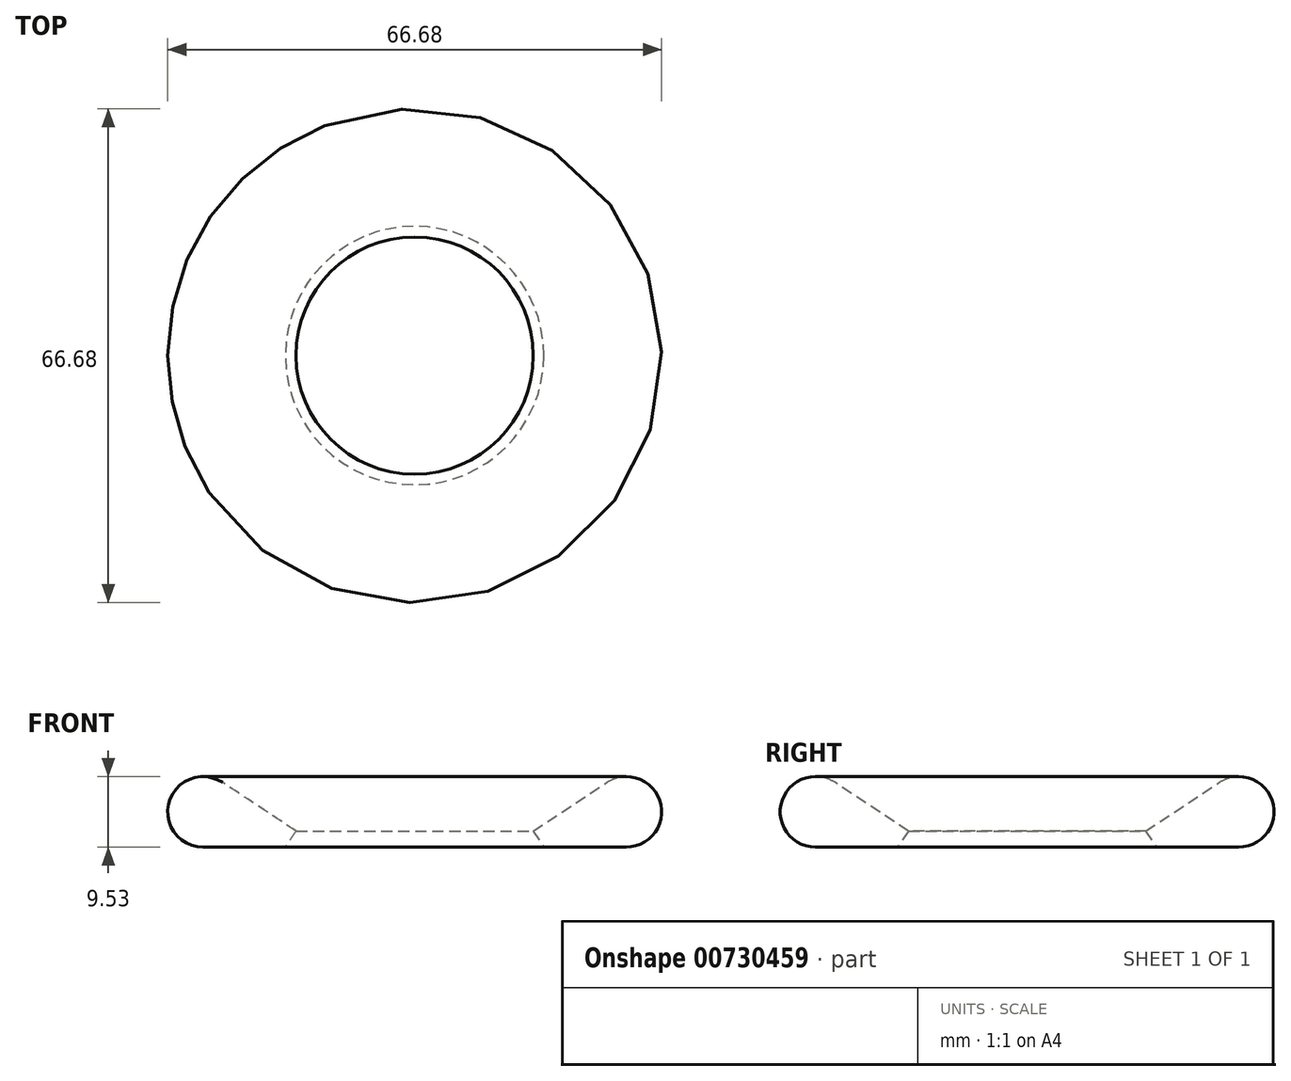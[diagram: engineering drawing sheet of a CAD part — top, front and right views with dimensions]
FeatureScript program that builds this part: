
annotation { "Feature Type Name" : "Feature", "Feature Type Description" : "" }
export const myFeature = defineFeature(function(context is Context, id is Id, definition is map)
    precondition{}
    {
        {
            var Q0;
            Q0=qCreatedBy(makeId("Front.planeOp"),FACE);
            var sketch = newSketch(context, id + "F0", { "sketchPlane" : qUnion([Q0])});
            skArc(sketch, "E0", {"start": v(28.58, 0) * mm, "mid": v(33.14, 6.13) * mm, "end": v(25.95, 8.74) * mm});
            skLineSegment(sketch, "E1", {"start": v(28.58, 0) * mm, "end": v(17.45, 0) * mm});
            skLineSegment(sketch, "E2", {"start": v(12.7, 0) * mm, "end": v(16.01, 2.18) * mm, "construction": true});
            skLineSegment(sketch, "E3", {"start": v(-29.35, 0) * mm, "end": v(13.91, 0) * mm, "construction": true});
            skLineSegment(sketch, "E4", {"start": v(16.01, 2.18) * mm, "end": v(17.45, 0) * mm});
            skLineSegment(sketch, "E5", {"start": v(16.01, 2.18) * mm, "end": v(25.95, 8.74) * mm});
            skLineSegment(sketch, "E6", {"start": v(17.45, 0) * mm, "end": v(12.7, 0) * mm, "construction": true});
            skLineSegment(sketch, "E7", {"start": v(0, 0) * mm, "end": v(0, 9.36) * mm, "construction": true});
            skSolve(sketch);
        }
        {
            var Q0;
            Q0=makeQuery(id+"F0.imprint","IMPRINT",FACE,{"disambiguationData":[TD([[makeQuery(id+"F0.imprint","IMPRINT",EDGE,{"derivedFrom":sQuery(id+"F0.wireOp",EDGE,"E0")}),1.0]])]});
            var Q1;
            Q1=sQuery(id+"F0.wireOp",EDGE,"E7");
            revolve(context, id + "F1", {"surfaceOperationType" : NewSurfaceOperationType.NEW, "entities" : qUnion([Q0]), "axis" : qUnion([Q1]), "revolveType" : RevolveType.FULL});
        }
    });
